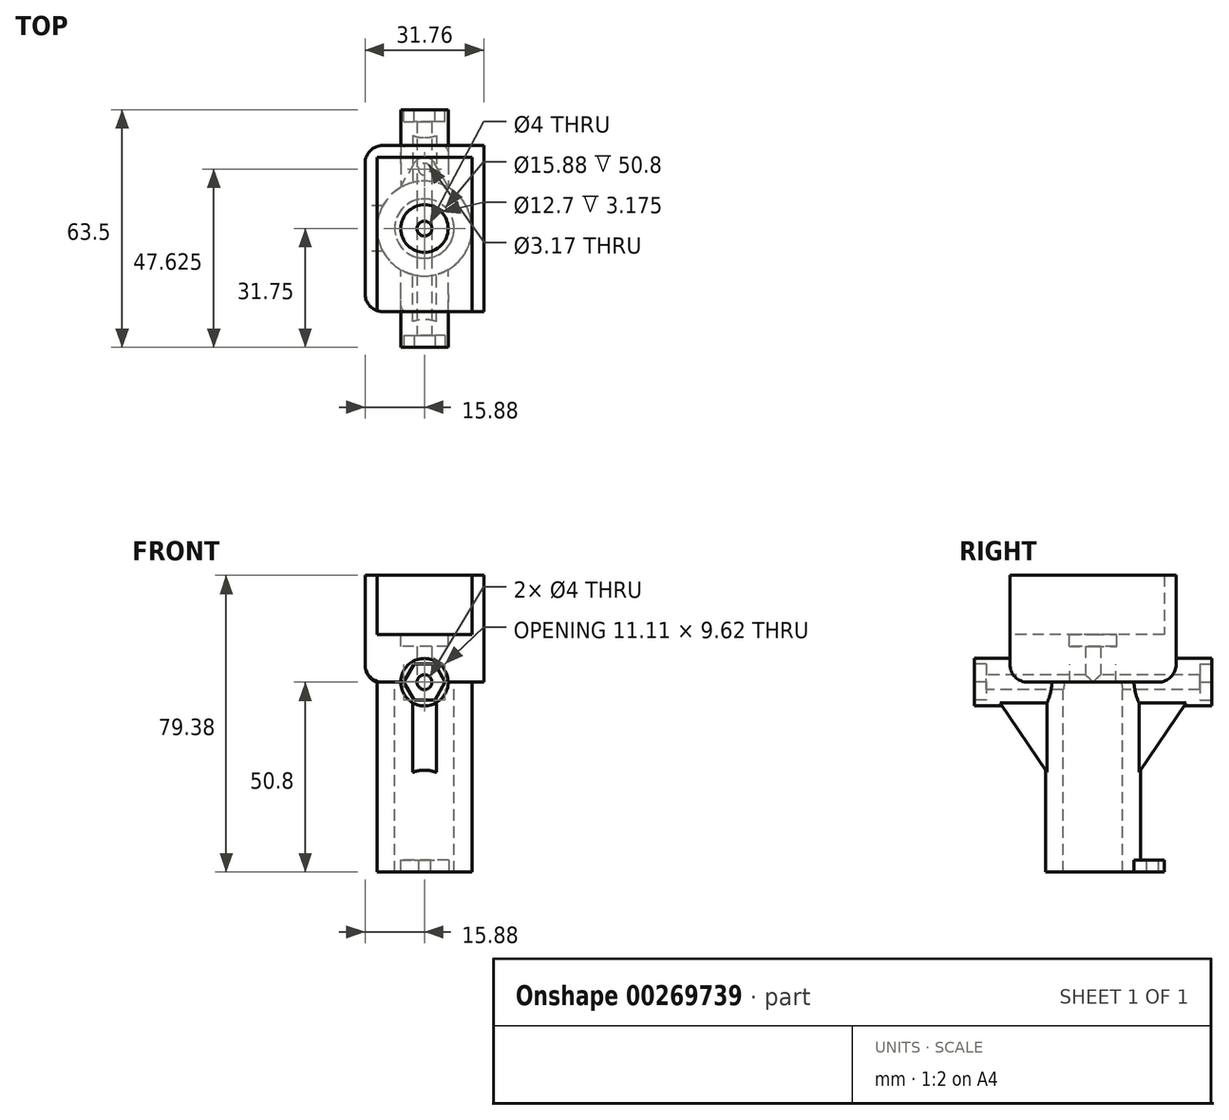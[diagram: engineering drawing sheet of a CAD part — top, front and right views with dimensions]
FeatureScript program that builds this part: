
annotation { "Feature Type Name" : "Feature", "Feature Type Description" : "" }
export const myFeature = defineFeature(function(context is Context, id is Id, definition is map)
    precondition{}
    {
        {
            var Q0;
            Q0=qCreatedBy(makeId("Top.planeOp"),FACE);
            var sketch = newSketch(context, id + "F0", { "sketchPlane" : qUnion([Q0])});
            skCircle(sketch, "E0", {"center": v(0, 0) * mm, "radius": 12.7 * mm});
            skCircle(sketch, "E1", {"center": v(0, 0) * mm, "radius": 7.94 * mm});
            skSolve(sketch);
        }
        {
            var Q0;
            Q0 = qSketchRegion(id + "F0", true);
            extrude(context, id + "F1", {"entities" : qUnion([Q0]), "oppositeDirection" : true, "depth" : 50.8 * mm});
        }
        {
            var Q0;
            Q0=qCreatedBy(makeId("Top.planeOp"),FACE);
            var sketch = newSketch(context, id + "F2", { "sketchPlane" : qUnion([Q0])});
            skCircle(sketch, "E2", {"center": v(0, 0) * mm, "radius": 2 * mm});
            skLineSegment(sketch, "E3.bottom", {"start": v(15.88, 22.23) * mm, "end": v(-15.88, 22.23) * mm});
            skLineSegment(sketch, "E3.top", {"start": v(15.88, -22.23) * mm, "end": v(-15.88, -22.23) * mm});
            skLineSegment(sketch, "E3.left", {"start": v(15.88, 22.22) * mm, "end": v(15.88, -22.23) * mm});
            skLineSegment(sketch, "E3.right", {"start": v(-15.88, 22.23) * mm, "end": v(-15.88, -22.23) * mm});
            skSolve(sketch);
        }
        {
            var Q0;
            Q0 = qSketchRegion(id + "F2", true);
            extrude(context, id + "F3", {"entities" : qUnion([Q0]), "operationType" : NewBodyOperationType.ADD, "depth" : 12.7 * mm});
        }
        {
            var Q0;
            Q0=qCreatedBy(makeId("Front.planeOp"),FACE);
            var sketch = newSketch(context, id + "F4", { "sketchPlane" : qUnion([Q0])});
            skCircle(sketch, "E4", {"center": v(0, 0) * mm, "radius": 6.35 * mm});
            skSolve(sketch);
        }
        {
            var Q0;
            Q0 = qSketchRegion(id + "F4", true);
            extrude(context, id + "F5", {"entities" : qUnion([Q0]), "operationType" : NewBodyOperationType.ADD, "depth" : 31.75 * mm, "hasSecondDirection" : true, "secondDirectionOppositeDirection" : false, "secondDirectionDepth" : 10.16 * mm});
        }
        {
            var Q0;
            Q0=qCreatedBy(makeId("Front.planeOp"),FACE);
            var sketch = newSketch(context, id + "F6", { "sketchPlane" : qUnion([Q0])});
            skCircle(sketch, "E5", {"center": v(0, 0) * mm, "radius": 6.35 * mm});
            skSolve(sketch);
        }
        {
            var Q0;
            Q0 = qSketchRegion(id + "F6", true);
            extrude(context, id + "F7", {"entities" : qUnion([Q0]), "operationType" : NewBodyOperationType.ADD, "oppositeDirection" : true, "depth" : 31.75 * mm, "hasSecondDirection" : true, "secondDirectionOppositeDirection" : true, "secondDirectionDepth" : 10.16 * mm});
        }
        {
            var Q0;
            Q0=makeQuery(id+"F5.opExtrude","CAP_FACE",FACE,{"disambiguationData":[OSD([sQuery(id+"F4.wireOp",EDGE,"E4")])],"isStart":false});
            var sketch = newSketch(context, id + "F8", { "sketchPlane" : qUnion([Q0])});
            skCircle(sketch, "E6", {"center": v(0, 0) * mm, "radius": 2 * mm});
            skSolve(sketch);
        }
        {
            var Q0;
            Q0 = qSketchRegion(id + "F8", true);
            extrude(context, id + "F9", {"entities" : qUnion([Q0]), "operationType" : NewBodyOperationType.REMOVE, "endBound" : BoundingType.THROUGH_ALL, "oppositeDirection" : true, "depth" : 19.05 * mm, "offsetDistance" : 25.4 * mm});
        }
        {
            var Q0;
            Q0=makeQuery(id+"F5.opExtrude","CAP_FACE",FACE,{"disambiguationData":[OSD([sQuery(id+"F4.wireOp",EDGE,"E4")])],"isStart":false});
            var sketch = newSketch(context, id + "F10", { "sketchPlane" : qUnion([Q0])});
            skCircle(sketch, "E7.cCircle", {"center": v(0, 0) * mm, "radius": 5.56 * mm, "construction": true});
            skLineSegment(sketch, "E7.0", {"start": v(5.56, 0) * mm, "end": v(2.78, -4.81) * mm});
            skLineSegment(sketch, "E7.1", {"start": v(2.78, -4.81) * mm, "end": v(-2.78, -4.81) * mm});
            skLineSegment(sketch, "E7.2", {"start": v(-2.78, -4.81) * mm, "end": v(-5.56, 0) * mm});
            skLineSegment(sketch, "E7.3", {"start": v(-5.56, 0) * mm, "end": v(-2.78, 4.81) * mm});
            skLineSegment(sketch, "E7.4", {"start": v(-2.78, 4.81) * mm, "end": v(2.78, 4.81) * mm});
            skLineSegment(sketch, "E7.5", {"start": v(2.78, 4.81) * mm, "end": v(5.56, 0) * mm});
            skSolve(sketch);
        }
        {
            var Q0;
            Q0 = qSketchRegion(id + "F10", true);
            extrude(context, id + "F11", {"entities" : qUnion([Q0]), "operationType" : NewBodyOperationType.REMOVE, "oppositeDirection" : true, "depth" : 3.17 * mm});
        }
        {
            var Q0;
            Q0=makeQuery(id+"F7.opExtrude","CAP_FACE",FACE,{"disambiguationData":[OSD([sQuery(id+"F6.wireOp",EDGE,"E5")])],"isStart":false});
            var sketch = newSketch(context, id + "F12", { "sketchPlane" : qUnion([Q0])});
            skCircle(sketch, "E8.cCircle", {"center": v(0, 0) * mm, "radius": 5.56 * mm, "construction": true});
            skLineSegment(sketch, "E8.0", {"start": v(5.56, 0) * mm, "end": v(2.78, -4.81) * mm});
            skLineSegment(sketch, "E8.1", {"start": v(2.78, -4.81) * mm, "end": v(-2.78, -4.81) * mm});
            skLineSegment(sketch, "E8.2", {"start": v(-2.78, -4.81) * mm, "end": v(-5.56, 0) * mm});
            skLineSegment(sketch, "E8.3", {"start": v(-5.56, 0) * mm, "end": v(-2.78, 4.81) * mm});
            skLineSegment(sketch, "E8.4", {"start": v(-2.78, 4.81) * mm, "end": v(2.78, 4.81) * mm});
            skLineSegment(sketch, "E8.5", {"start": v(2.78, 4.81) * mm, "end": v(5.56, 0) * mm});
            skSolve(sketch);
        }
        {
            var Q0;
            Q0 = qSketchRegion(id + "F12", true);
            extrude(context, id + "F13", {"entities" : qUnion([Q0]), "operationType" : NewBodyOperationType.REMOVE, "oppositeDirection" : true, "depth" : 3.17 * mm});
        }
        {
            var Q0;
            Q0=qCreatedBy(makeId("Right.planeOp"),FACE);
            var sketch = newSketch(context, id + "F14", { "sketchPlane" : qUnion([Q0])});
            skLineSegment(sketch, "E9.left", {"start": v(11.43, -4.76) * mm, "end": v(11.43, -25.4) * mm});
            skLineSegment(sketch, "E9.right", {"start": v(-11.43, -4.76) * mm, "end": v(-11.43, -25.4) * mm});
            skPoint(sketch, "E9.middle", {"position": v(0, 0) * mm});
            skLineSegment(sketch, "E10.top", {"start": v(25.4, -4.76) * mm, "end": v(11.43, -4.76) * mm});
            skLineSegment(sketch, "E11", {"start": v(-25.4, -4.76) * mm, "end": v(-11.43, -25.4) * mm});
            skLineSegment(sketch, "E12", {"start": v(11.43, -25.4) * mm, "end": v(25.4, -4.76) * mm});
            skLineSegment(sketch, "E13.trimOffspring", {"start": v(-11.43, -4.76) * mm, "end": v(-25.4, -4.76) * mm});
            skSolve(sketch);
        }
        {
            var Q0;
            Q0 = qSketchRegion(id + "F14", true);
            extrude(context, id + "F15", {"entities" : qUnion([Q0]), "operationType" : NewBodyOperationType.ADD, "endBound" : BoundingType.SYMMETRIC, "depth" : 6.35 * mm});
        }
        {
            var Q0;
            Q0=makeQuery(id+"F3.opExtrude","CAP_FACE",FACE,{"disambiguationData":[OSD([sQuery(id+"F2.wireOp",EDGE,"E2"),sQuery(id+"F2.wireOp",EDGE,"E3.bottom"),sQuery(id+"F2.wireOp",EDGE,"E3.top"),sQuery(id+"F2.wireOp",EDGE,"E3.left"),sQuery(id+"F2.wireOp",EDGE,"E3.right")])],"isStart":false});
            var sketch = newSketch(context, id + "F16", { "sketchPlane" : qUnion([Q0])});
            skLineSegment(sketch, "E14.bottom", {"start": v(15.88, 22.23) * mm, "end": v(-15.88, 22.23) * mm});
            skLineSegment(sketch, "E14.top", {"start": v(15.88, -22.23) * mm, "end": v(-15.88, -22.23) * mm});
            skLineSegment(sketch, "E14.left", {"start": v(15.88, 22.23) * mm, "end": v(15.88, -22.23) * mm});
            skLineSegment(sketch, "E14.right", {"start": v(-15.88, 22.23) * mm, "end": v(-15.88, -22.23) * mm});
            skPoint(sketch, "E14.middle", {"position": v(0, 0) * mm});
            skLineSegment(sketch, "E15.bottom", {"start": v(12.7, 19.05) * mm, "end": v(-12.7, 19.05) * mm});
            skLineSegment(sketch, "E15.top", {"start": v(12.7, -19.05) * mm, "end": v(-12.7, -19.05) * mm});
            skLineSegment(sketch, "E15.left", {"start": v(12.7, 19.05) * mm, "end": v(12.7, -19.05) * mm});
            skLineSegment(sketch, "E15.right", {"start": v(-12.7, 19.05) * mm, "end": v(-12.7, -19.05) * mm});
            skSolve(sketch);
        }
        {
            var Q0;
            Q0 = qSketchRegion(id + "F16", true);
            extrude(context, id + "F17", {"entities" : qUnion([Q0]), "operationType" : NewBodyOperationType.ADD, "depth" : 15.88 * mm, "offsetDistance" : 25.4 * mm});
        }
        {
            var Q0;
            Q0=makeQuery(id+"F3.opExtrude","CAP_FACE",FACE,{"disambiguationData":[OSD([sQuery(id+"F2.wireOp",EDGE,"E2"),sQuery(id+"F2.wireOp",EDGE,"E3.bottom"),sQuery(id+"F2.wireOp",EDGE,"E3.top"),sQuery(id+"F2.wireOp",EDGE,"E3.left"),sQuery(id+"F2.wireOp",EDGE,"E3.right")])],"isStart":false});
            var sketch = newSketch(context, id + "F18", { "sketchPlane" : qUnion([Q0])});
            skCircle(sketch, "E16", {"center": v(0, 0) * mm, "radius": 6.35 * mm});
            skSolve(sketch);
        }
        {
            var Q0;
            Q0 = qSketchRegion(id + "F18", true);
            extrude(context, id + "F19", {"entities" : qUnion([Q0]), "operationType" : NewBodyOperationType.REMOVE, "oppositeDirection" : true, "depth" : 3.17 * mm});
        }
        {
            var Q0;
            {var subQ0=sQuery(id+"F0.wireOp",EDGE,"E0");var subQ1=sQuery(id+"F2.wireOp",EDGE,"E3.left");Q0=makeQuery(id+"F5.boolean.opBoolean","SPLIT",EDGE,{"disambiguationData":[TD([makeQuery(id+"F3.opExtrude","SWEPT_FACE",FACE,{"disambiguationData":[OSD([subQ1])]})])],"derivedFrom":makeQuery(id+"F3.boolean.opBoolean","SPLIT",EDGE,{"disambiguationData":[OD(1.0)],"derivedFrom":makeQuery(id+"F1.opExtrude","CAP_EDGE",EDGE,{"disambiguationData":[OSD([subQ0])],"isStart":true})})});}
            var Q1;
            {var subQ0=sQuery(id+"F0.wireOp",EDGE,"E0");var subQ1=sQuery(id+"F2.wireOp",EDGE,"E3.right");Q1=makeQuery(id+"F5.boolean.opBoolean","SPLIT",EDGE,{"disambiguationData":[TD([makeQuery(id+"F3.opExtrude","SWEPT_FACE",FACE,{"disambiguationData":[OSD([subQ1])]})])],"derivedFrom":makeQuery(id+"F3.boolean.opBoolean","SPLIT",EDGE,{"disambiguationData":[OD(1.0)],"derivedFrom":makeQuery(id+"F1.opExtrude","CAP_EDGE",EDGE,{"disambiguationData":[OSD([subQ0])],"isStart":true})})});}
            var Q2;
            {var subQ0=sQuery(id+"F2.wireOp",EDGE,"E3.left");var subQ1=sQuery(id+"F2.wireOp",EDGE,"E3.top");Q2=makeQuery(id+"F5.boolean.opBoolean","SPLIT",EDGE,{"disambiguationData":[TD([makeQuery(id+"F3.opExtrude","SWEPT_FACE",FACE,{"disambiguationData":[OSD([subQ0])]})])],"derivedFrom":makeQuery(id+"F3.opExtrude","CAP_EDGE",EDGE,{"disambiguationData":[OSD([subQ1])],"isStart":true})});}
            var Q3;
            {var subQ0=sQuery(id+"F2.wireOp",EDGE,"E3.right");var subQ1=sQuery(id+"F2.wireOp",EDGE,"E3.top");Q3=makeQuery(id+"F5.boolean.opBoolean","SPLIT",EDGE,{"disambiguationData":[TD([makeQuery(id+"F3.opExtrude","SWEPT_FACE",FACE,{"disambiguationData":[OSD([subQ0])]})])],"derivedFrom":makeQuery(id+"F3.opExtrude","CAP_EDGE",EDGE,{"disambiguationData":[OSD([subQ1])],"isStart":true})});}
            var Q4;
            {var subQ0=sQuery(id+"F2.wireOp",EDGE,"E3.left");var subQ1=sQuery(id+"F2.wireOp",EDGE,"E3.bottom");Q4=makeQuery(id+"F7.boolean.opBoolean","SPLIT",EDGE,{"disambiguationData":[TD([makeQuery(id+"F3.opExtrude","SWEPT_FACE",FACE,{"disambiguationData":[OSD([subQ0])]})])],"derivedFrom":makeQuery(id+"F3.opExtrude","CAP_EDGE",EDGE,{"disambiguationData":[OSD([subQ1])],"isStart":true})});}
            var Q5;
            {var subQ0=sQuery(id+"F2.wireOp",EDGE,"E3.right");var subQ1=sQuery(id+"F2.wireOp",EDGE,"E3.bottom");Q5=makeQuery(id+"F7.boolean.opBoolean","SPLIT",EDGE,{"disambiguationData":[TD([makeQuery(id+"F3.opExtrude","SWEPT_FACE",FACE,{"disambiguationData":[OSD([subQ0])]})])],"derivedFrom":makeQuery(id+"F3.opExtrude","CAP_EDGE",EDGE,{"disambiguationData":[OSD([subQ1])],"isStart":true})});}
            fillet(context, id + "F20", {"entities" : qUnion([Q0, Q1, Q2, Q3, Q4, Q5]), "radius" : 4.76 * mm, "tangentPropagation" : true, "allowEdgeOverflow" : false});
        }
        {
            var Q0;
            Q0=makeQuery(id+"F1.opExtrude","CAP_FACE",FACE,{"disambiguationData":[OSD([sQuery(id+"F0.wireOp",EDGE,"E0"),sQuery(id+"F0.wireOp",EDGE,"E1")])],"isStart":false});
            var sketch = newSketch(context, id + "F21", { "sketchPlane" : qUnion([Q0])});
            skPoint(sketch, "E17.orphan", {"position": v(-14.31, 0) * mm});
            skPoint(sketch, "E18.orphan", {"position": v(-6.43, -31.72) * mm});
            skPoint(sketch, "E19.center.orphan", {"position": v(0, -31.72) * mm});
            skArc(sketch, "E20", {"start": v(-2.76, -17.45) * mm, "mid": v(0, -19.05) * mm, "end": v(2.76, -17.45) * mm});
            skLineSegment(sketch, "E21", {"start": v(-6.47, -10.93) * mm, "end": v(-2.76, -17.45) * mm});
            skLineSegment(sketch, "E22", {"start": v(6.47, -10.93) * mm, "end": v(2.76, -17.45) * mm});
            skArc(sketch, "E23", {"start": v(-6.47, -10.93) * mm, "mid": v(0, -12.7) * mm, "end": v(6.47, -10.93) * mm});
            skCircle(sketch, "E24", {"center": v(0, 0) * mm, "radius": 15.88 * mm, "construction": true});
            skLineSegment(sketch, "E25", {"start": v(0, -12.7) * mm, "end": v(-9.53, -12.7) * mm, "construction": true});
            skLineSegment(sketch, "E26", {"start": v(0, -12.7) * mm, "end": v(9.52, -12.7) * mm, "construction": true});
            skLineSegment(sketch, "E27", {"start": v(0, 0) * mm, "end": v(-9.53, -12.7) * mm, "construction": true});
            skLineSegment(sketch, "E28", {"start": v(0, 0) * mm, "end": v(0, -15.88) * mm, "construction": true});
            skCircle(sketch, "E29", {"center": v(0, -15.88) * mm, "radius": 1.59 * mm});
            skSolve(sketch);
        }
        {
            var Q0;
            Q0 = qSketchRegion(id + "F21", true);
            extrude(context, id + "F22", {"entities" : qUnion([Q0]), "operationType" : NewBodyOperationType.ADD, "oppositeDirection" : true, "depth" : 3.17 * mm});
        }
        {
            var Q0;
            Q0=makeQuery(id+"F17.boolean.opBoolean","MERGE",FACE,{"derivedFrom":[makeQuery(id+"F3.opExtrude","SWEPT_FACE",FACE,{"disambiguationData":[OSD([sQuery(id+"F2.wireOp",EDGE,"E3.top")])]}),makeQuery(id+"F17.opExtrude","SWEPT_FACE",FACE,{"disambiguationData":[OSD([sQuery(id+"F16.wireOp",EDGE,"E14.top")])]})]});
            var sketch = newSketch(context, id + "F23", { "sketchPlane" : qUnion([Q0])});
            skLineSegment(sketch, "E30.bottom", {"start": v(-12.7, 12.7) * mm, "end": v(12.7, 12.7) * mm});
            skLineSegment(sketch, "E30.top", {"start": v(-12.7, 28.58) * mm, "end": v(12.7, 28.58) * mm});
            skLineSegment(sketch, "E30.left", {"start": v(-12.7, 12.7) * mm, "end": v(-12.7, 28.58) * mm});
            skLineSegment(sketch, "E30.right", {"start": v(12.7, 12.7) * mm, "end": v(12.7, 28.58) * mm});
            skSolve(sketch);
        }
        {
            var Q0;
            Q0 = qSketchRegion(id + "F23", true);
            extrude(context, id + "F24", {"entities" : qUnion([Q0]), "operationType" : NewBodyOperationType.REMOVE, "oppositeDirection" : true, "depth" : 6.35 * mm, "offsetDistance" : 25.4 * mm});
        }
        {
            var Q0;
            Q0=makeQuery(id+"F20.opFillet","BLEND_EDGE",EDGE,{"blendedFrom":[makeQuery(id+"F7.boolean.opBoolean","SPLIT",EDGE,{"disambiguationData":[OD(0.0)],"derivedFrom":makeQuery(id+"F1.opExtrude","CAP_EDGE",EDGE,{"disambiguationData":[OSD([sQuery(id+"F0.wireOp",EDGE,"E0")])],"isStart":true})}),makeQuery(id+"F17.boolean.opBoolean","MERGE",FACE,{"derivedFrom":[makeQuery(id+"F3.opExtrude","SWEPT_FACE",FACE,{"disambiguationData":[OSD([sQuery(id+"F2.wireOp",EDGE,"E3.left")])]}),makeQuery(id+"F17.opExtrude","SWEPT_FACE",FACE,{"disambiguationData":[OSD([sQuery(id+"F16.wireOp",EDGE,"E14.left")])]})]})],"blendedInto":[makeQuery(id+"F17.boolean.opBoolean","MERGE",FACE,{"derivedFrom":[makeQuery(id+"F3.opExtrude","SWEPT_FACE",FACE,{"disambiguationData":[OSD([sQuery(id+"F2.wireOp",EDGE,"E3.left")])]}),makeQuery(id+"F17.opExtrude","SWEPT_FACE",FACE,{"disambiguationData":[OSD([sQuery(id+"F16.wireOp",EDGE,"E14.left")])]})]})]});
            var Q1;
            Q1=makeQuery(id+"F3.opExtrude","CAP_EDGE",EDGE,{"disambiguationData":[OSD([sQuery(id+"F2.wireOp",EDGE,"E3.right")])],"isStart":true});
            fillet(context, id + "F25", {"entities" : qUnion([Q0, Q1]), "radius" : 4.76 * mm, "tangentPropagation" : true, "allowEdgeOverflow" : false});
        }
    });
